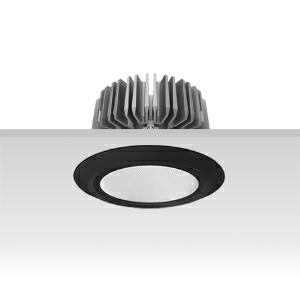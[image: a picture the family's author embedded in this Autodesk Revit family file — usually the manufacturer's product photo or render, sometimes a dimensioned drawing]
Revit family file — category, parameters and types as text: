
# Revit family: 3f_filippi_-_3f_reno_bianco_ampio_3f_filippi_-_30366_a01047_-_3f_reno_150_wh_3000-840_ep_wide___smp_bk_72d9
name_source: partatom
category: Lighting Fixtures
units: mm (PartAtom-declared; Revit-internal decimal feet)

## family parameters
Cut with Voids When Loaded = No
Host = Face
Light Source = No
Part Type = Normal
Room Calculation Point = No
Round Connector Dimension = Use Diameter
Shared = No

## types (1)
- 3F Filippi - 3F Reno Bianco Ampio (1 x LED, 2316 lm, 29 W, 4000 K)
    Apparent Load = 29 VA
    Approval mark = ENEC
    CIE Flux Codes = 73 92 98 100 100
    Color Rendering = 80
    Color Temperature = 4000 K
    Control Gear = Electronic ballast
    Default Elevation = 1800 mm
    Description = ILLUMINOTECHNICAL
Luminous efficiency 100% (DLOR 100%, ULOR 0%).
Initial luminous flux of the luminaire 2316 lm.
Emergency luminaire luminous flux BLF 14.3%.
Direct symmetric wide distribution.
Installation Interdistance Transv.D = 1.01 x hu - Long.D = 1.00 x hu.
Tabular UGR (CIE 117 - 4H-8H; S=0.25H; 70/50/20): RUG 24.4 - 24.5.
Beam angle: 70° - 70°.
Luminous efficacy 80 lm/W.
Lifetime (L90/B10): 30000 h. (tq+25°C)
Lifetime (L85/B10): 50000 h. (tq+25°C)
Lifetime (L70/B10): 80000 h. (tq+25°C)
Sudden decreased luminous flux after 50000 hours: 0% (C0).
Photobiological safety in compliance with IEC/TR 62778: RG0 risk exempt, (IEC 62471).
In compliance with IEC/EN 62722-2-1 - IEC/EN 62717 standards.

SOURCE
Compact LED module 3000/840.
Energy efficiency class (UE 2019/2020 - UE 2019/2015): D.
CIE 13.3 Colour rendering index: CRI >80 (R9 <50%).
IES TM-30 Fidelity Index: Rf = 84 Rg = 95.
CCT nominal colour temperature 4000 K.
Colour initial tolerance (MacAdam): SDCM 3.
Zhaga Book 3 compliant.

MECHANICAL
Passive heat dissipator in die-casting aluminium, oversized, for optimum thermal management of the LED module.
Parabolic element with graduated/concentric rings in white polycarbonate.
Transparent external lens with glossy and satin differentiated surfaces, with a cooling and anti-insect system in methacrylate (PMMA).
Fastening spring clips in stainless steel.
Dimensions: diameter 176 mm, height 111 mm. Weight 1.94 kg.
IP44 protection degree for exposed part, IP20 for recessed part.
Mechanical strength to impacts IK05 (0.7 joule).
Glow-wire test resistance 650°C.

ELECTRICAL
Wiring on a separate unit.
Halogen Free electronic wiring 230V-50/60Hz, power factor 0.90, THD <25%, constant output current, SELV, class II, 1 driver.
Power of the luminaire 29 W.
CE - IEC 60598-1 - EN 60598-1.
EP maintained emergency wiring on board, 1h duration, 24h recharge; compliant with EN 60598-2-22, excluding high risk areas.
SAFE FLICKER: PstLM=<1 and SVM=<0.4 (IEC TR 61547-1 and IEC TR 63158), to ensure a more comfortable and safe light.
Ambient temperature from +5°C to +25°C.
Temperature class T6 max 85°C.
Relative humidity UR: <85%.

INSTALLATION
Pull-up recessed fitting.
False ceiling carving: 150 mm.
All accessories dedicated to this product are available on the Catalog and on our website www.3F-Filippi.com.

ACCESSORIES
A01047 - Anti-glare microprismatic SMP diffuser in methacrylate (PMMA), locked and in line with the trim, in black polycarbonate.

APPLICATIONS
Suitable product for food production plants (HACCP), IFS (Food Version 6), BRC (GSFS Food Version 7).
Environments: architectural, commercial, exhibition areas, transit areas, corridors, shops, display windows, service areas.
In false ceilings with narrow voids.

WARNING
Luminaire designed for disposal/recycling at end-of-life.
Replaceable (LED only) light source by a professional. Replaceable control gear by a professional.
    Height = 0 mm  [stored 0 ft]
    Lamp = 1 x LED
    Lamp Light Flux = 2316 lm
    Lamp Power = 29 W
    Lamp count = 1
    Length = 176 mm
    Lifetime = 50000 h
    Luminous efficacy = 80 lm/W
    Manufacturer = 3F Filippi
    ModVariant = No
    Model = 3F Filippi - 30366+A01047 - 3F Reno 150 WH 3000-840 EP WIDE + SMP BK
    Mounting Place = Ceiling
    Mounting Type = Recessed
    Number of Poles = 1
    OnlyDefault = Yes
    Power Factor = 1
    Product Name = 3F Filippi - 3F Reno Bianco Ampio
    Product group = recessed luminaire
    ProductGroupID = 4
    Protection Class = Protection class II
    Protection Degree = IP 20
    RLX_Detail_Level = 1
    RLX_Emergency_Light_Flux = 0 lm
    RLX_Emergency_Type = 0
    RLX_Emergency_Type_DB = No
    RlxData = <blob elided: 85541 chars, md5=eec7783d>
    Socket = socket
    Standby Power = 0 W
    System Light Flux = 2316 lm
    System Power = 29 W
    Type Comments = Product without accessories
    Type Image = 3ffilippi_3f_reno_150_bk_vs_smp.jpg
    URL = http://relux.com
    VarID = ---
    Voltage = 0 V
    Weight = 0.00 kg
    Width = 0 mm  [stored 0 ft]

note: [stored X ft] marks values corroborated as IEEE doubles in the binary element streams (Revit-internal decimal feet)

## geometry (parser evidence)
native form markers: Blend x4, Sweep x10
no freeform markers — native parametric forms only
